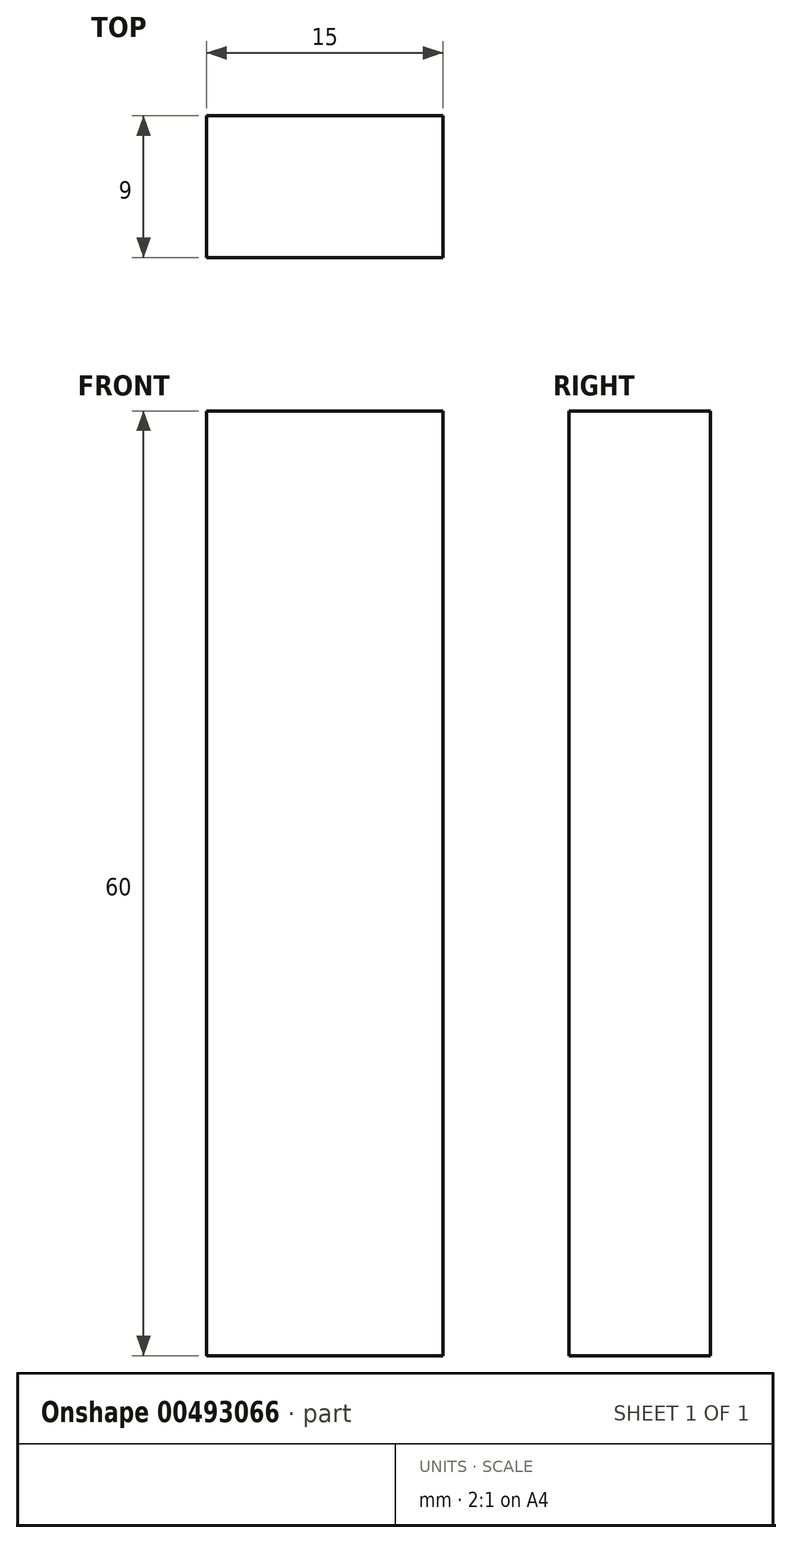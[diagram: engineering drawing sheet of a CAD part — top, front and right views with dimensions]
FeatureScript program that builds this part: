
annotation { "Feature Type Name" : "Feature", "Feature Type Description" : "" }
export const myFeature = defineFeature(function(context is Context, id is Id, definition is map)
    precondition{}
    {
        {
            var Q0;
            Q0=qCreatedBy(makeId("Top.planeOp"),FACE);
            var sketch = newSketch(context, id + "F0", { "sketchPlane" : qUnion([Q0])});
            skLineSegment(sketch, "E0.bottom", {"start": v(7.5, -4.5) * mm, "end": v(-7.5, -4.5) * mm});
            skLineSegment(sketch, "E0.top", {"start": v(7.5, 4.5) * mm, "end": v(-7.5, 4.5) * mm});
            skLineSegment(sketch, "E0.left", {"start": v(7.5, -4.5) * mm, "end": v(7.5, 4.5) * mm});
            skLineSegment(sketch, "E0.right", {"start": v(-7.5, -4.5) * mm, "end": v(-7.5, 4.5) * mm});
            skPoint(sketch, "E0.middle", {"position": v(0, 0) * mm});
            skSolve(sketch);
        }
        {
            var Q0;
            Q0 = qSketchRegion(id + "F0", true);
            extrude(context, id + "F1", {"entities" : qUnion([Q0]), "endBound" : BoundingType.SYMMETRIC, "depth" : 60 * mm});
        }
    });
